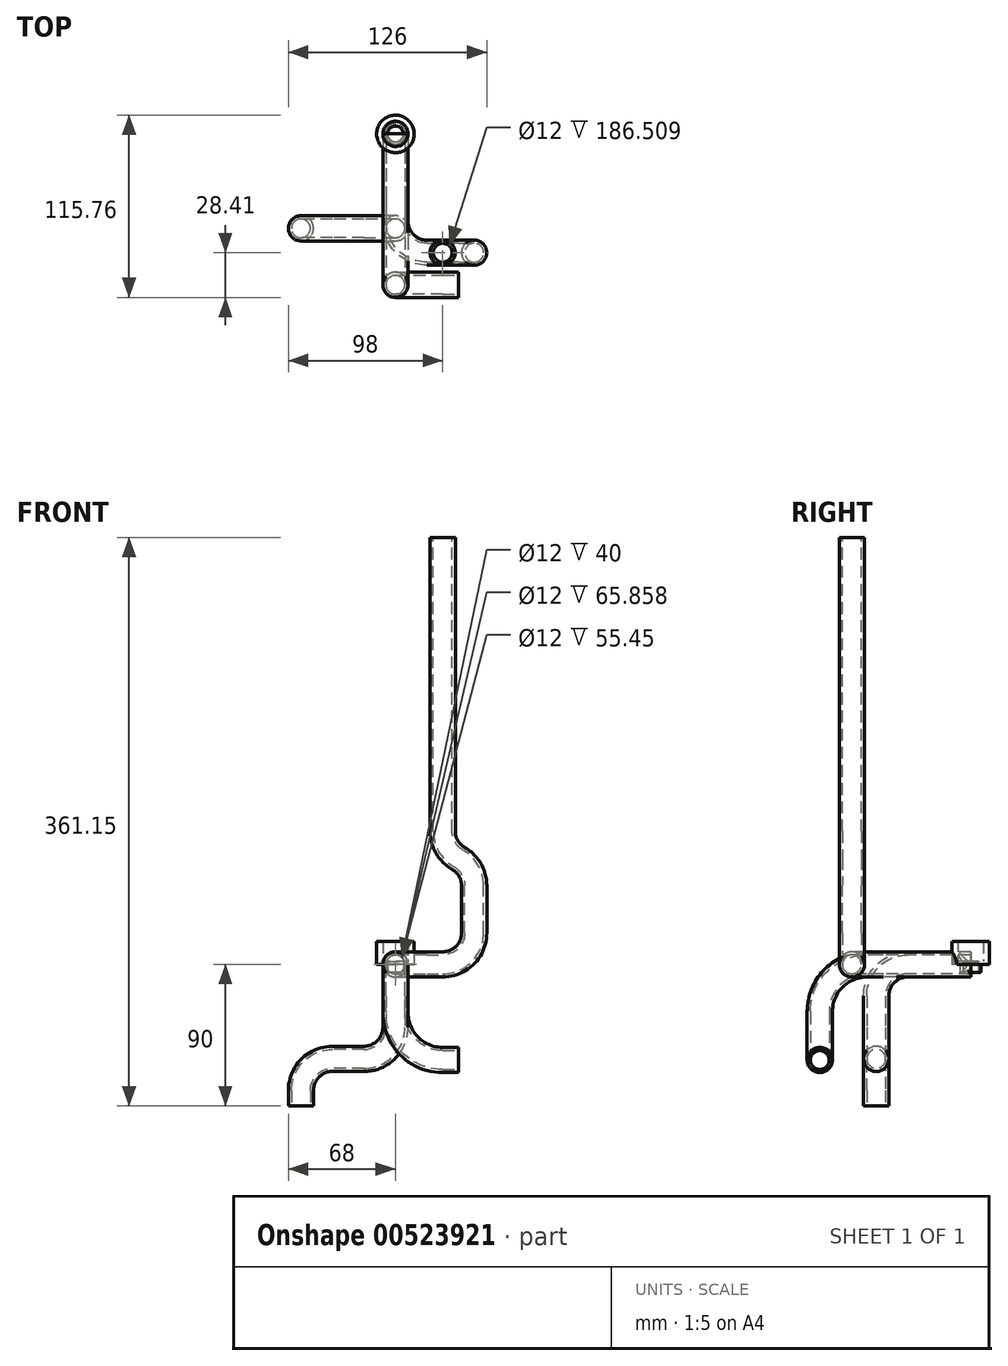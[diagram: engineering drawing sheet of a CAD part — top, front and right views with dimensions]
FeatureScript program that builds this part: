
annotation { "Feature Type Name" : "Feature", "Feature Type Description" : "" }
export const myFeature = defineFeature(function(context is Context, id is Id, definition is map)
    precondition{}
    {
        {
            var Q0;
            Q0=qCreatedBy(makeId("Front.planeOp"),FACE);
            var sketch = newSketch(context, id + "F0", { "sketchPlane" : qUnion([Q0])});
            skCircle(sketch, "E0", {"center": v(0, 0) * mm, "radius": 8 * mm});
            skCircle(sketch, "E1", {"center": v(0, 0) * mm, "radius": 6 * mm});
            skSolve(sketch);
        }
        {
            var Q0;
            Q0=qCreatedBy(makeId("Right.planeOp"),FACE);
            var sketch = newSketch(context, id + "F1", { "sketchPlane" : qUnion([Q0])});
            skLineSegment(sketch, "E2", {"start": v(0, 0) * mm, "end": v(-65.86, 0) * mm});
            skLineSegment(sketch, "E3", {"start": v(-95.86, -30) * mm, "end": v(-95.86, -30) * mm});
            skPoint(sketch, "E4.visualSharp", {"position": v(-95.86, 0) * mm});
            skArc(sketch, "E4.filletArc", {"start": v(-65.86, 0) * mm, "mid": v(-87.07, -8.79) * mm, "end": v(-95.86, -30) * mm});
            skSolve(sketch);
        }
        {
            var Q0;
            Q0=qSketchRegion(id+"F0",true);
            var Q1;
            Q1=qConstructionFilter(qBodyType(qCreatedBy(id+"F1",EDGE),BodyType.WIRE),ConstructionObject.NO);
            sweep(context, id + "F2", {"profiles" : qUnion([Q0]), "path" : qUnion([Q1])});
        }
        {
            var Q0;
            Q0=qCreatedBy(makeId("Top.planeOp"),FACE);
            var sketch = newSketch(context, id + "F3", { "sketchPlane" : qUnion([Q0])});
            skCircle(sketch, "E5", {"center": v(0, 0) * mm, "radius": 11.9 * mm});
            skCircle(sketch, "E6", {"center": v(0, 0) * mm, "radius": 8 * mm});
            skSolve(sketch);
        }
        {
            var Q0;
            Q0=qSketchRegion(id+"F3",true);
            extrude(context, id + "F4", {"entities" : qUnion([Q0]), "depth" : 14.5 * mm});
        }
        {
            var Q0;
            Q0=makeQuery(id+"F4.opExtrude","CAP_FACE",FACE,{"disambiguationData":[OSD([sQuery(id+"F3.wireOp",EDGE,"E5"),sQuery(id+"F3.wireOp",EDGE,"E6")])],"isStart":true});
            var sketch = newSketch(context, id + "F5", { "sketchPlane" : qUnion([Q0])});
            skCircle(sketch, "E7", {"center": v(0, 0) * mm, "radius": 5 * mm});
            skCircle(sketch, "E8", {"center": v(0, 0) * mm, "radius": 8 * mm});
            skSolve(sketch);
        }
        {
            var Q0;
            Q0=qSketchRegion(id+"F5",true);
            extrude(context, id + "F6", {"entities" : qUnion([Q0]), "operationType" : NewBodyOperationType.ADD, "oppositeDirection" : true, "depth" : 2 * mm});
        }
        {
            var Q0;
            Q0=makeQuery(id+"F6.boolean.opBoolean","MERGE",FACE,{"derivedFrom":[makeQuery(id+"F4.opExtrude","CAP_FACE",FACE,{"disambiguationData":[OSD([sQuery(id+"F3.wireOp",EDGE,"E5"),sQuery(id+"F3.wireOp",EDGE,"E6")])],"isStart":true}),makeQuery(id+"F6.opExtrude","CAP_FACE",FACE,{"disambiguationData":[OSD([sQuery(id+"F5.wireOp",EDGE,"E7"),sQuery(id+"F5.wireOp",EDGE,"E8")])],"isStart":true})]});
            var sketch = newSketch(context, id + "F7", { "sketchPlane" : qUnion([Q0])});
            skCircle(sketch, "E9", {"center": v(0, 0) * mm, "radius": 5 * mm});
            skCircle(sketch, "E10", {"center": v(0, 0) * mm, "radius": 6.5 * mm});
            skSolve(sketch);
        }
        {
            var Q0;
            Q0=qSketchRegion(id+"F7",true);
            extrude(context, id + "F8", {"entities" : qUnion([Q0]), "operationType" : NewBodyOperationType.ADD, "depth" : 5 * mm});
        }
        {
            var Q0;
            Q0=qCreatedBy(makeId("Front.planeOp"),FACE);
            cPlane(context, id + "F9", {"entities" : qUnion([Q0]), "cplaneType" : CPlaneType.OFFSET, "offset" : (100 - 1.72 - 2.42) * mm, "width" : 150 * mm, "height" : 150 * mm});
        }
        {
            var Q0;
            Q0=qCreatedBy(id+"F9.planeOp",FACE);
            var sketch = newSketch(context, id + "F10", { "sketchPlane" : qUnion([Q0])});
            skLineSegment(sketch, "E11", {"start": v(0, -30) * mm, "end": v(0, -30.76) * mm});
            skLineSegment(sketch, "E12", {"start": v(30, -60.76) * mm, "end": v(40, -60.76) * mm});
            skPoint(sketch, "E13.visualSharp", {"position": v(0, -60.76) * mm});
            skArc(sketch, "E13.filletArc", {"start": v(0, -30.76) * mm, "mid": v(8.79, -51.98) * mm, "end": v(30, -60.76) * mm});
            skSolve(sketch);
        }
        {
            var Q0;
            Q0=makeQuery(id+"F2.opSweep","CAP_FACE",FACE,{"disambiguationData":[OSD([sQuery(id+"F0.wireOp",EDGE,"E0"),sQuery(id+"F0.wireOp",EDGE,"E1"),sQuery(id+"F1.wireOp",VERTEX,"E3.end")])],"isStart":false});
            var Q1;
            Q1=qConstructionFilter(qBodyType(qCreatedBy(id+"F10",EDGE),BodyType.WIRE),ConstructionObject.NO);
            sweep(context, id + "F11", {"operationType" : NewBodyOperationType.ADD, "profiles" : qUnion([Q0]), "path" : qUnion([Q1])});
        }
        {
            var Q0;
            Q0=qCreatedBy(makeId("Front.planeOp"),FACE);
            var sketch = newSketch(context, id + "F12", { "sketchPlane" : qUnion([Q0])});
            skCircle(sketch, "E14", {"center": v(0, 0) * mm, "radius": 6 * mm});
            skCircle(sketch, "E15", {"center": v(0, 0) * mm, "radius": 8 * mm});
            skSolve(sketch);
        }
        {
            var Q0;
            Q0=qCreatedBy(makeId("Top.planeOp"),FACE);
            var sketch = newSketch(context, id + "F13", { "sketchPlane" : qUnion([Q0])});
            skLineSegment(sketch, "E16", {"start": v(0, 0) * mm, "end": v(0, -55.45) * mm});
            skLineSegment(sketch, "E17", {"start": v(20, -75.45) * mm, "end": v(25, -75.45) * mm});
            skPoint(sketch, "E18.visualSharp", {"position": v(0, -75.45) * mm});
            skArc(sketch, "E18.filletArc", {"start": v(0, -55.45) * mm, "mid": v(5.86, -69.6) * mm, "end": v(20, -75.45) * mm});
            skSolve(sketch);
        }
        {
            var Q0;
            Q0=qCreatedBy(makeId("Front.planeOp"),FACE);
            cPlane(context, id + "F14", {"entities" : qUnion([Q0]), "cplaneType" : CPlaneType.OFFSET, "offset" : 75.45 * mm, "width" : 150 * mm, "height" : 150 * mm});
        }
        {
            var Q0;
            Q0=qCreatedBy(id+"F14.planeOp",FACE);
            var sketch = newSketch(context, id + "F15", { "sketchPlane" : qUnion([Q0])});
            skLineSegment(sketch, "E19", {"start": v(25, 0) * mm, "end": v(30, 0) * mm});
            skLineSegment(sketch, "E20", {"start": v(50, 20) * mm, "end": v(50, 50) * mm});
            skPoint(sketch, "E21.visualSharp", {"position": v(50, 0) * mm});
            skArc(sketch, "E21.filletArc", {"start": v(30, 0) * mm, "mid": v(44.14, 5.86) * mm, "end": v(50, 20) * mm});
            skSolve(sketch);
        }
        {
            var Q0;
            Q0=qSketchRegion(id+"F12",true);
            var Q1;
            Q1=qConstructionFilter(qBodyType(qCreatedBy(id+"F13",EDGE),BodyType.WIRE),ConstructionObject.NO);
            sweep(context, id + "F16", {"profiles" : qUnion([Q0]), "path" : qUnion([Q1])});
        }
        {
            var Q0;
            Q0=makeQuery(id+"F16.opSweep","CAP_FACE",FACE,{"disambiguationData":[OSD([sQuery(id+"F12.wireOp",EDGE,"E14"),sQuery(id+"F12.wireOp",EDGE,"E15"),sQuery(id+"F13.wireOp",VERTEX,"E17.end")])],"isStart":false});
            var Q1;
            Q1=qConstructionFilter(qBodyType(qCreatedBy(id+"F15",EDGE),BodyType.WIRE),ConstructionObject.NO);
            sweep(context, id + "F17", {"operationType" : NewBodyOperationType.ADD, "profiles" : qUnion([Q0]), "path" : qUnion([Q1])});
        }
        {
            var Q0;
            Q0=qCreatedBy(id+"F14.planeOp",FACE);
            var sketch = newSketch(context, id + "F18", { "sketchPlane" : qUnion([Q0])});
            skArc(sketch, "E22", {"start": v(50, 50) * mm, "mid": v(47.32, 60) * mm, "end": v(40, 67.32) * mm});
            skLineSegment(sketch, "E23", {"start": v(50, 50) * mm, "end": v(50, 16.4) * mm, "construction": true});
            skArc(sketch, "E24", {"start": v(30, 84.64) * mm, "mid": v(32.68, 74.64) * mm, "end": v(40, 67.32) * mm});
            skLineSegment(sketch, "E25", {"start": v(30, 84.64) * mm, "end": v(30, 271.15) * mm});
            skSolve(sketch);
        }
        {
            var Q0;
            Q0=makeQuery(id+"F17.opSweep","CAP_FACE",FACE,{"disambiguationData":[OSD([sQuery(id+"F12.wireOp",EDGE,"E14"),sQuery(id+"F12.wireOp",EDGE,"E15"),sQuery(id+"F13.wireOp",VERTEX,"E17.end"),sQuery(id+"F15.wireOp",VERTEX,"E20.end")])],"isStart":false});
            var Q1;
            Q1=qConstructionFilter(qBodyType(qCreatedBy(id+"F18",EDGE),BodyType.WIRE),ConstructionObject.NO);
            sweep(context, id + "F19", {"operationType" : NewBodyOperationType.ADD, "profiles" : qUnion([Q0]), "path" : qUnion([Q1])});
        }
        {
            var Q0;
            Q0=qCreatedBy(makeId("Front.planeOp"),FACE);
            var sketch = newSketch(context, id + "F20", { "sketchPlane" : qUnion([Q0])});
            skCircle(sketch, "E26", {"center": v(0, 0) * mm, "radius": 6 * mm});
            skCircle(sketch, "E27", {"center": v(0, 0) * mm, "radius": 8 * mm});
            skSolve(sketch);
        }
        {
            var Q0;
            Q0=qCreatedBy(makeId("Right.planeOp"),FACE);
            var sketch = newSketch(context, id + "F21", { "sketchPlane" : qUnion([Q0])});
            skLineSegment(sketch, "E28", {"start": v(0, 0) * mm, "end": v(-40, 0) * mm});
            skLineSegment(sketch, "E29", {"start": v(-60, -20) * mm, "end": v(-60, -40) * mm});
            skPoint(sketch, "E30.visualSharp", {"position": v(-60, 0) * mm});
            skArc(sketch, "E30.filletArc", {"start": v(-40, 0) * mm, "mid": v(-54.14, -5.86) * mm, "end": v(-60, -20) * mm});
            skSolve(sketch);
        }
        {
            var Q0;
            Q0=qSketchRegion(id+"F20",true);
            var Q1;
            Q1=qConstructionFilter(qBodyType(qCreatedBy(id+"F21",EDGE),BodyType.WIRE),ConstructionObject.NO);
            sweep(context, id + "F22", {"profiles" : qUnion([Q0]), "path" : qUnion([Q1])});
        }
        {
            var Q0;
            Q0=qCreatedBy(makeId("Front.planeOp"),FACE);
            cPlane(context, id + "F23", {"entities" : qUnion([Q0]), "cplaneType" : CPlaneType.OFFSET, "offset" : 40 * mm, "width" : 150 * mm, "height" : 150 * mm});
        }
        {
            var Q0;
            Q0=qCreatedBy(id+"F23.planeOp",FACE);
            var sketch = newSketch(context, id + "F24", { "sketchPlane" : qUnion([Q0])});
            skLineSegment(sketch, "E31", {"start": v(0, -40) * mm, "end": v(0, -40) * mm});
            skLineSegment(sketch, "E32", {"start": v(-20, -60) * mm, "end": v(-40, -60) * mm});
            skPoint(sketch, "E33.visualSharp", {"position": v(0, -60) * mm});
            skArc(sketch, "E33.filletArc", {"start": v(-20, -60) * mm, "mid": v(-5.86, -54.14) * mm, "end": v(0, -40) * mm});
            skLineSegment(sketch, "E34", {"start": v(-60, -80) * mm, "end": v(-60, -90) * mm});
            skPoint(sketch, "E35.visualSharp", {"position": v(-60, -60) * mm});
            skArc(sketch, "E35.filletArc", {"start": v(-40, -60) * mm, "mid": v(-54.14, -65.86) * mm, "end": v(-60, -80) * mm});
            skSolve(sketch);
        }
        {
            var Q0;
            Q0=makeQuery(id+"F22.opSweep","CAP_FACE",FACE,{"disambiguationData":[OSD([sQuery(id+"F20.wireOp",EDGE,"E26"),sQuery(id+"F20.wireOp",EDGE,"E27"),sQuery(id+"F21.wireOp",VERTEX,"E29.end")])],"isStart":false});
            var Q1;
            Q1=qConstructionFilter(qBodyType(qCreatedBy(id+"F24",EDGE),BodyType.WIRE),ConstructionObject.NO);
            sweep(context, id + "F25", {"operationType" : NewBodyOperationType.ADD, "profiles" : qUnion([Q0]), "path" : qUnion([Q1])});
        }
    });
